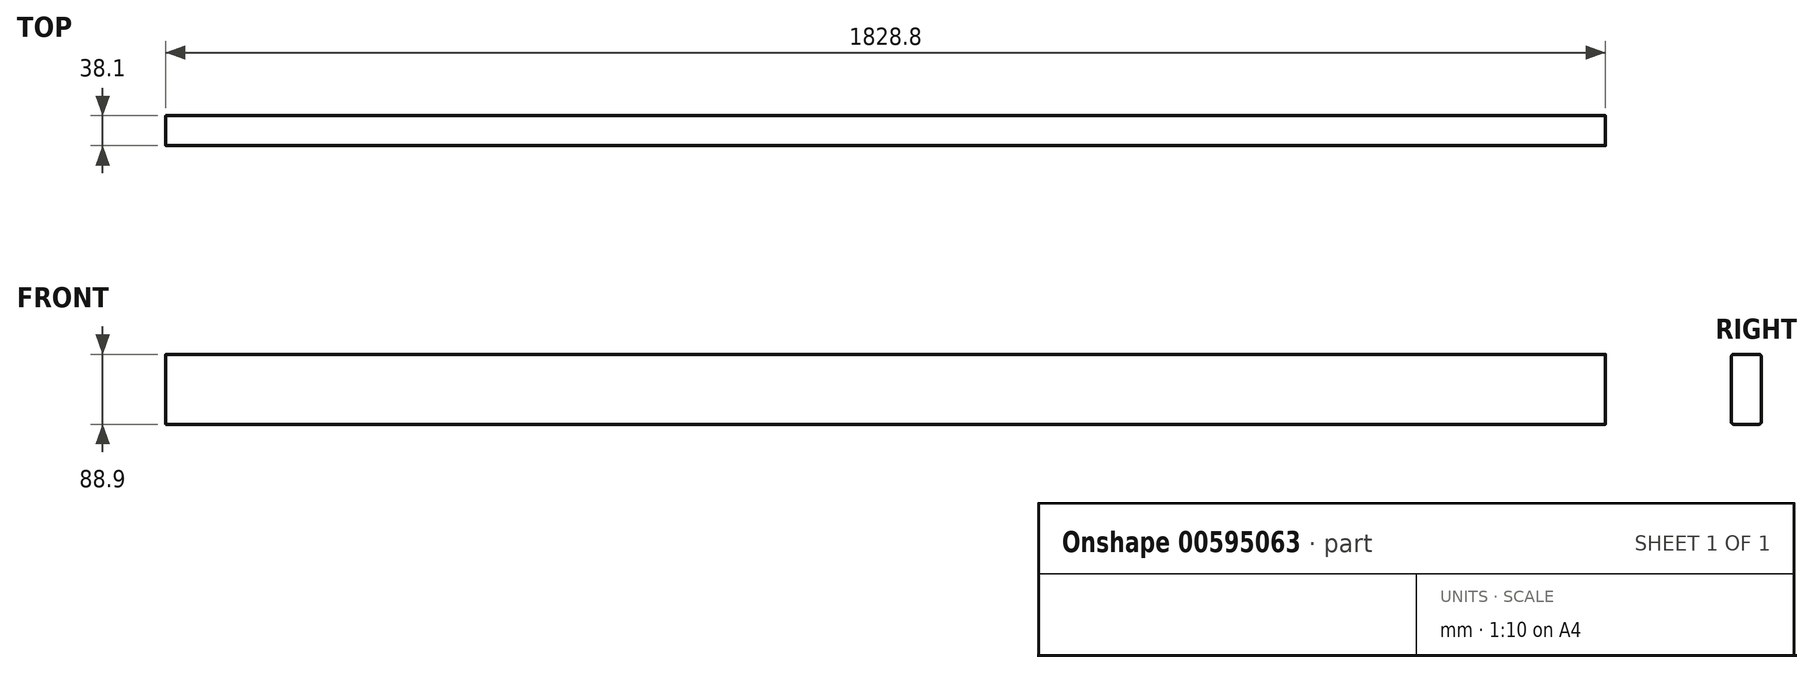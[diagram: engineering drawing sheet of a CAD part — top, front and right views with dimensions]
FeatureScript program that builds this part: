
annotation { "Feature Type Name" : "Feature", "Feature Type Description" : "" }
export const myFeature = defineFeature(function(context is Context, id is Id, definition is map)
    precondition{}
    {
        {
            var Q0;
            Q0=qCreatedBy(makeId("Right.planeOp"),FACE);
            var sketch = newSketch(context, id + "F0", { "sketchPlane" : qUnion([Q0])});
            skLineSegment(sketch, "E0.bottom", {"start": v(-19.05, 44.45) * mm, "end": v(19.05, 44.45) * mm});
            skLineSegment(sketch, "E0.top", {"start": v(-19.05, -44.45) * mm, "end": v(19.05, -44.45) * mm});
            skLineSegment(sketch, "E0.left", {"start": v(-19.05, 44.45) * mm, "end": v(-19.05, -44.45) * mm});
            skLineSegment(sketch, "E0.right", {"start": v(19.05, 44.45) * mm, "end": v(19.05, -44.45) * mm});
            skPoint(sketch, "E0.middle", {"position": v(0, 0) * mm});
            skSolve(sketch);
        }
        {
            var Q0;
            Q0 = qSketchRegion(id + "F0", true);
            extrude(context, id + "F1", {"entities" : qUnion([Q0]), "endBound" : BoundingType.SYMMETRIC, "depth" : 1828.8 * mm, "offsetDistance" : 25.4 * mm});
        }
        {
            var Q0;
            Q0=makeQuery(id+"F1.opExtrude","SWEPT_EDGE",EDGE,{"disambiguationData":[OSD([sQuery(id+"F0.wireOp",EDGE,"E0.bottom"),sQuery(id+"F0.wireOp",EDGE,"E0.left")])]});
            var Q1;
            Q1=makeQuery(id+"F1.opExtrude","SWEPT_EDGE",EDGE,{"disambiguationData":[OSD([sQuery(id+"F0.wireOp",EDGE,"E0.bottom"),sQuery(id+"F0.wireOp",EDGE,"E0.right")])]});
            var Q2;
            Q2=makeQuery(id+"F1.opExtrude","SWEPT_EDGE",EDGE,{"disambiguationData":[OSD([sQuery(id+"F0.wireOp",EDGE,"E0.top"),sQuery(id+"F0.wireOp",EDGE,"E0.left")])]});
            var Q3;
            Q3=makeQuery(id+"F1.opExtrude","SWEPT_EDGE",EDGE,{"disambiguationData":[OSD([sQuery(id+"F0.wireOp",EDGE,"E0.top"),sQuery(id+"F0.wireOp",EDGE,"E0.right")])]});
            fillet(context, id + "F2", {"entities" : qUnion([Q0, Q1, Q2, Q3]), "radius" : 3.17 * mm, "tangentPropagation" : true, "allowEdgeOverflow" : false});
        }
    });
